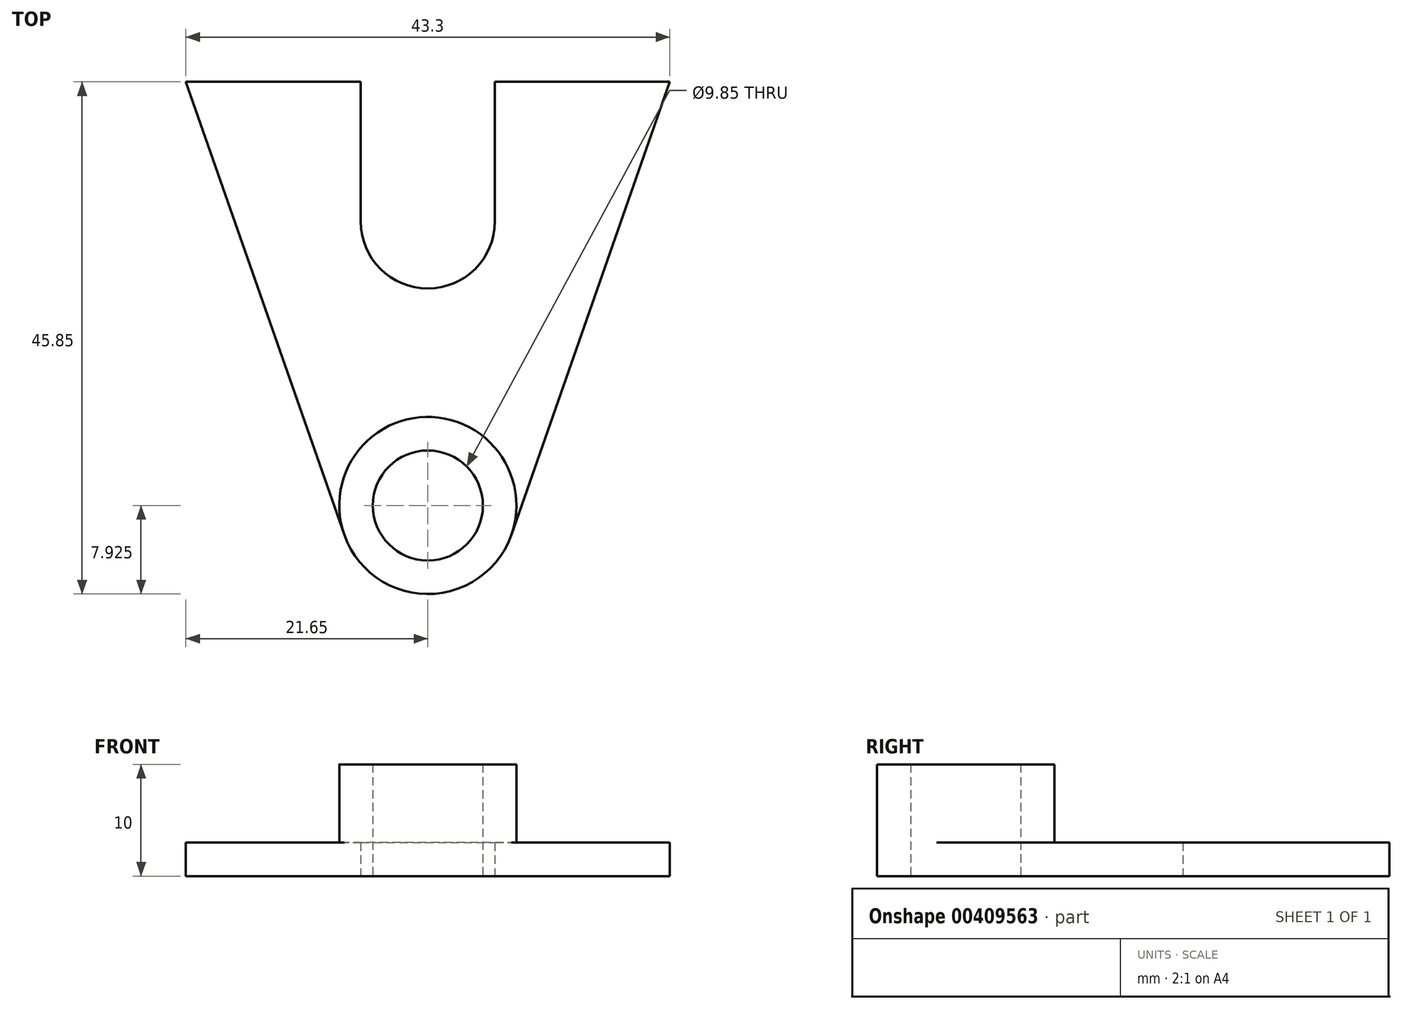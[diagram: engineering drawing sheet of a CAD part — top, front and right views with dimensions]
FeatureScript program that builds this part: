
annotation { "Feature Type Name" : "Feature", "Feature Type Description" : "" }
export const myFeature = defineFeature(function(context is Context, id is Id, definition is map)
    precondition{}
    {
        {
            var Q0;
            Q0=qCreatedBy(makeId("Top.planeOp"),FACE);
            var sketch = newSketch(context, id + "F0", { "sketchPlane" : qUnion([Q0])});
            skCircle(sketch, "E0.cCircle", {"center": v(0, 0) * mm, "radius": 12.5 * mm, "construction": true});
            skLineSegment(sketch, "E0.2", {"start": v(-21.65, 12.5) * mm, "end": v(-6, 12.5) * mm});
            skPoint(sketch, "E0.0.midPoint", {"position": v(10.83, -6.25) * mm});
            skPoint(sketch, "E1", {"position": v(-16.65, 12.5) * mm});
            skPoint(sketch, "E2", {"position": v(-19.15, 8.17) * mm});
            skArc(sketch, "E3", {"start": v(-6, 0) * mm, "mid": v(0, -6) * mm, "end": v(6, 0) * mm});
            skLineSegment(sketch, "E4", {"start": v(-6, 0) * mm, "end": v(-6, 12.5) * mm});
            skLineSegment(sketch, "E5", {"start": v(6, 0) * mm, "end": v(6, 12.5) * mm});
            skCircle(sketch, "E6", {"center": v(0, -25.43) * mm, "radius": 4.92 * mm});
            skCircle(sketch, "E7.0", {"center": v(0, -25.43) * mm, "radius": 7.92 * mm});
            skLineSegment(sketch, "E8", {"start": v(21.65, 12.5) * mm, "end": v(7.48, -28.04) * mm});
            skLineSegment(sketch, "E9", {"start": v(-21.65, 12.5) * mm, "end": v(-7.48, -28.04) * mm});
            skPoint(sketch, "E10.orphan", {"position": v(0, -25) * mm});
            skPoint(sketch, "E11.orphan", {"position": v(-12.5, 12.5) * mm});
            skLineSegment(sketch, "E12.trimOffspring", {"start": v(6, 12.5) * mm, "end": v(21.65, 12.5) * mm});
            skSolve(sketch);
        }
        {
            var Q0;
            Q0=makeQuery(id+"F0.imprint","IMPRINT",FACE,{"disambiguationData":[TD([[makeQuery(id+"F0.imprint","IMPRINT",EDGE,{"derivedFrom":sQuery(id+"F0.wireOp",EDGE,"E6")}),-1.0]])]});
            extrude(context, id + "F1", {"entities" : qUnion([Q0]), "depth" : 10 * mm});
        }
        {
            var Q0;
            Q0=makeQuery(id+"F0.imprint","IMPRINT",FACE,{"disambiguationData":[TD([[makeQuery(id+"F0.imprint","IMPRINT",EDGE,{"derivedFrom":sQuery(id+"F0.wireOp",EDGE,"E0.2")}),-1.0]])]});
            extrude(context, id + "F2", {"entities" : qUnion([Q0]), "operationType" : NewBodyOperationType.ADD, "depth" : 3 * mm});
        }
    });
